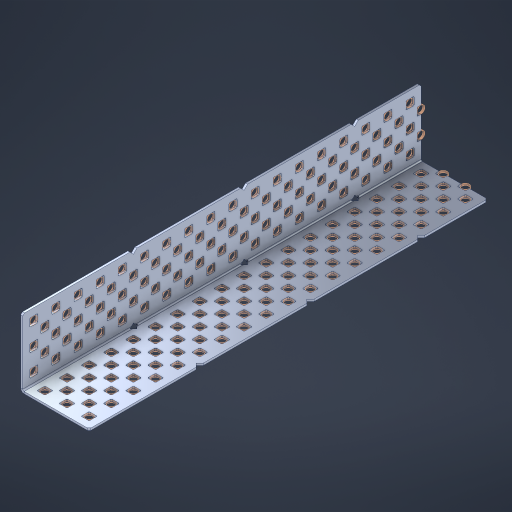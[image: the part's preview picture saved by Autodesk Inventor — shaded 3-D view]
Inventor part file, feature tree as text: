
AUTODESK INVENTOR PART (.ipt)
format: ipt  version: 2023 (Build 270158000, 158)  size: 2,013,184 bytes
history: native  units: in
note: dims shown in document units (in); Inventor stores cm internally (conversion verified against a paired STEP export)
features: other x186, extrude x178, sheet_metal_op x8, sketch x7, pattern_linear x3, mirror x1, chamfer x1
ambient origin geometry x8: Origin, YZ Plane, XZ Plane, XY Plane, X Axis, Y Axis, Z Axis, Center Point
bodies: Solid1 (feature_tree), Body (feature_tree)
feature tree (384):
  sheet_metal_op  "Flanges"
  sheet_metal_op  "Body Pattern"
  pattern_linear  "Center Double"  Spacing1=1.5in  [1 undecoded]
  pattern_linear  "Center Pattern"  Spacing1=0.1875in  [1 undecoded]
  other  "Arc Length"
  pattern_linear  "Notch Pattern"  Spacing1=0.0469in  [1 undecoded]
  other  "Diagonal Plane"
  mirror  "Everything Mirrored"
  chamfer  "End Chamfer"
  sketch  "Sketch1"  dims[d0=1.5in]
  other  "Plate1"
  sketch  "Sketch2"  dims[d1=9.0in]
  other  "Plate2"
  sheet_metal_op  "Bend1"
  sheet_metal_op  "Corner1"
  sketch  "Sketch8"  dims[d2=0.0469in]
  sketch  "Sketch9"  dims[d3=0.0469in]
  other  "Srf91"
  sheet_metal_op  "Body Pattern Sketch"
  other  "Srf92"
  sketch  "Sketch13"  dims[d4=0.0234in]
  sketch  "Sketch15"  dims[d5=0.0938in]
  sketch  "Sketch16"  dims[d6=0.0469in d7=1.5in d8=90.0deg d9=0.0312in d10=0.1875in d11=0.0469in d12=0.0469in d49=0.182in d50=0.02in d52=0.25in d53=0.0469in d54=0.0in d55=0.172in d56=1.0in d57=0.0in d85=0.1473in d86=0.1659in d89=0.0469in d90=0.0in d91=0.04in d92=0.0491in d95=2.5in d96=0.04in d97=0.25in d98=45.0deg d106=0.182in d107=0.02in d110=0.0469in d111=0.0in d112=0.172in d113=0.5in d114=0.0in d117=0.5in d126=0.0491in d127=0.1227in d128=0.08in d129=0.04in d130=2.5in d131=0.25in d132=7.0866in d134=0.5in d135=1.1811in d137=0.5in d140=0.5in d141=1.0in d142=0.3937in d144=0.5in d145=0.071in d146=0.7874in d148=0.5in]
  other  "Srf786"
  other  "Srf856"
  other  "Srf889"
  other  "Srf890"
  other  "Srf891"
  other  "Srf1275"
  other  "Srf1276"
  other  "Srf1278"
  other  "Srf1277"
  other  "Srf1285"
  other  "Srf1286"
  other  "Srf1287"
  other  "Srf1445"
  other  "Srf1446"
  other  "Srf1447"
  other  "Srf1448"
  other  "Srf1449"
  other  "Srf1537"
  other  "Srf1538"
  other  "Srf1539"
  other  "Srf1540"
  other  "Srf1541"
  other  "Srf1807"
  other  "Srf1808"
  other  "Srf1809"
  other  "Srf1810"
  other  "Srf1811"
  other  "Srf1812"
  other  "Srf1813"
  other  "Srf1814"
  other  "Srf1815"
  other  "Srf1959"
  other  "Srf1960"
  other  "Srf1961"
  other  "Srf1962"
  other  "Srf1963"
  other  "Srf1964"
  other  "Srf1965"
  other  "Srf1966"
  other  "Srf1967"
  other  "Srf2009"
  other  "Srf2010"
  other  "Srf2011"
  other  "Srf2012"
  other  "Srf2013"
  other  "Srf2014"
  other  "Srf2015"
  other  "Srf2016"
  other  "Srf2017"
  other  "Srf2018"
  other  "Srf2019"
  other  "Srf2020"
  other  "Srf2021"
  other  "Srf2022"
  other  "Srf2023"
  other  "Srf2024"
  other  "Srf2025"
  other  "Srf2026"
  other  "Srf2043"
  other  "Srf2044"
  other  "Srf2045"
  other  "Srf2046"
  other  "Srf2047"
  other  "Srf2048"
  other  "Srf2049"
  other  "Srf2050"
  other  "Srf2051"
  other  "Srf2052"
  other  "Srf2053"
  other  "Srf2054"
  other  "Srf2055"
  other  "Srf2056"
  other  "Srf2057"
  other  "Srf2058"
  other  "Srf2059"
  other  "Srf2076"
  other  "Srf2077"
  other  "Srf2078"
  other  "Srf2079"
  other  "Srf2080"
  other  "Srf2081"
  other  "Srf2082"
  other  "Srf2083"
  other  "Srf2084"
  other  "Srf2085"
  other  "Srf2086"
  other  "Srf2087"
  other  "Srf2088"
  other  "Srf2089"
  other  "Srf2090"
  other  "Srf2091"
  other  "Srf2092"
  other  "Srf2093"
  other  "Srf2094"
  other  "Srf2095"
  other  "Srf2096"
  other  "Srf2097"
  other  "Srf2098"
  other  "Srf2099"
  other  "Srf2100"
  other  "Srf2101"
  other  "Srf2102"
  other  "Srf2103"
  other  "Srf2104"
  other  "Srf2105"
  other  "Srf2106"
  other  "Srf2107"
  other  "Srf2108"
  other  "Srf2109"
  other  "Srf2110"
  other  "Srf2111"
  other  "Srf2112"
  other  "Srf2113"
  other  "Srf2114"
  other  "Srf2115"
  other  "Srf2116"
  other  "Srf2117"
  other  "Srf2118"
  other  "Srf2119"
  other  "Srf2120"
  other  "Srf2121"
  other  "Srf2122"
  other  "Srf2123"
  other  "Srf2124"
  other  "Srf2125"
  other  "Srf2126"
  other  "Srf2127"
  other  "Srf2179"
  other  "Srf2180"
  other  "Srf2181"
  other  "Srf2182"
  other  "Srf2183"
  other  "Srf2184"
  other  "Srf2185"
  other  "Srf2186"
  other  "Srf2187"
  other  "Srf2188"
  other  "Srf2189"
  other  "Srf2190"
  other  "Srf2191"
  other  "Srf2192"
  other  "Srf2193"
  other  "Srf2194"
  other  "Srf2195"
  other  "Srf2196"
  other  "Srf2197"
  other  "Srf2198"
  other  "Srf2199"
  other  "Srf2200"
  other  "Srf2201"
  other  "Srf2202"
  other  "Srf2203"
  other  "Srf2204"
  other  "Srf2205"
  other  "Srf2206"
  other  "Srf2207"
  other  "Srf2208"
  other  "Srf2209"
  other  "Srf2210"
  other  "Srf2211"
  other  "Srf2212"
  other  "Srf2213"
  other  "Srf2214"
  other  "Srf2215"
  other  "Srf2216"
  other  "Srf2217"
  other  "Srf2218"
  other  "Srf2219"
  other  "Srf2220"
  other  "Srf2221"
  other  "Srf2222"
  other  "Srf2223"
  other  "Srf2224"
  other  "Srf2225"
  other  "Srf2226"
  other  "Srf2227"
  other  "Srf2228"
  other  "Srf2229"
  sheet_metal_op  "Body Stamp"
  sheet_metal_op  "Body Circle"
  other  "Center Stamp"
  other  "Center Circle"
  sheet_metal_op  "Notch"
  extrude  "ExtrusionSrf92"  Depth=0.0469in
  extrude  "ExtrusionSrf856"  Depth=0.182in
  extrude  "ExtrusionSrf889"  Depth=0.02in
  extrude  "ExtrusionSrf890"  Depth=0.25in
  extrude  "ExtrusionSrf891"  Depth=0.0469in
  extrude  "ExtrusionSrf1275"  TaperAngle=0.0deg  [1 undecoded]
  extrude  "ExtrusionSrf1276"  Depth=0.5in
  extrude  "ExtrusionSrf1277"  Depth=1.0in TaperAngle=0.0deg
  extrude  "ExtrusionSrf1345"  Depth=0.5in
  extrude  "ExtrusionSrf1346"  Depth=0.5in
  extrude  "ExtrusionSrf1347"  Depth=0.0469in
  extrude  "ExtrusionSrf1348"  Depth=0.5in TaperAngle=0.0deg
  extrude  "ExtrusionSrf1445"  Depth=0.5in
  extrude  "ExtrusionSrf1446"  Depth=0.25in TaperAngle=45.0deg
  extrude  "ExtrusionSrf1447"  Depth=0.182in
  extrude  "ExtrusionSrf1448"  Depth=0.02in
  extrude  "ExtrusionSrf1449"  Depth=0.0469in
  extrude  "ExtrusionSrf1537"  TaperAngle=0.0deg  [1 undecoded]
  extrude  "ExtrusionSrf1538"  Depth=0.5in
  extrude  "ExtrusionSrf1539"  Depth=0.5in TaperAngle=0.0deg
  extrude  "ExtrusionSrf1540"  Depth=0.5in
  extrude  "ExtrusionSrf1541"  Depth=0.5in
  extrude  "ExtrusionSrf1807"  Depth=0.5in
  extrude  "ExtrusionSrf1808"  Depth=0.5in
  extrude  "ExtrusionSrf1809"  Depth=0.5in
  extrude  "ExtrusionSrf1810"  Depth=0.5in
  extrude  "ExtrusionSrf1811"  Depth=0.25in
  extrude  "ExtrusionSrf1812"  Depth=0.5in
  extrude  "ExtrusionSrf1813"  Depth=0.5in
  extrude  "ExtrusionSrf1814"  Depth=0.5in
  extrude  "ExtrusionSrf1815"  Depth=1.0in
  extrude  "ExtrusionSrf1959"  Depth=0.3937in
  extrude  "ExtrusionSrf1960"  Depth=0.5in
  extrude  "ExtrusionSrf1961"  Depth=0.5in
  extrude  "ExtrusionSrf1962"  [1 undecoded]
  extrude  "ExtrusionSrf1963"  [1 undecoded]
  extrude  "ExtrusionSrf1964"  [1 undecoded]
  extrude  "ExtrusionSrf1965"  [1 undecoded]
  extrude  "ExtrusionSrf1966"  [1 undecoded]
  extrude  "ExtrusionSrf1967"  [1 undecoded]
  extrude  "ExtrusionSrf2009"  [1 undecoded]
  extrude  "ExtrusionSrf2010"  [1 undecoded]
  extrude  "ExtrusionSrf2011"  [1 undecoded]
  extrude  "ExtrusionSrf2012"  [1 undecoded]
  extrude  "ExtrusionSrf2013"  [1 undecoded]
  extrude  "ExtrusionSrf2014"  [1 undecoded]
  extrude  "ExtrusionSrf2015"  [1 undecoded]
  extrude  "ExtrusionSrf2016"  [1 undecoded]
  extrude  "ExtrusionSrf2017"  [1 undecoded]
  extrude  "ExtrusionSrf2018"  [1 undecoded]
  extrude  "ExtrusionSrf2019"  [1 undecoded]
  extrude  "ExtrusionSrf2020"  [1 undecoded]
  extrude  "ExtrusionSrf2021"  [1 undecoded]
  extrude  "ExtrusionSrf2022"  [1 undecoded]
  extrude  "ExtrusionSrf2023"  [1 undecoded]
  extrude  "ExtrusionSrf2024"  [1 undecoded]
  extrude  "ExtrusionSrf2025"  [1 undecoded]
  extrude  "ExtrusionSrf2026"  [1 undecoded]
  extrude  "ExtrusionSrf2043"  [1 undecoded]
  extrude  "ExtrusionSrf2044"  [1 undecoded]
  extrude  "ExtrusionSrf2045"  [1 undecoded]
  extrude  "ExtrusionSrf2046"  [1 undecoded]
  extrude  "ExtrusionSrf2047"  [1 undecoded]
  extrude  "ExtrusionSrf2048"  [1 undecoded]
  extrude  "ExtrusionSrf2049"  [1 undecoded]
  extrude  "ExtrusionSrf2050"  [1 undecoded]
  extrude  "ExtrusionSrf2051"  [1 undecoded]
  extrude  "ExtrusionSrf2052"  [1 undecoded]
  extrude  "ExtrusionSrf2053"  [1 undecoded]
  extrude  "ExtrusionSrf2054"  [1 undecoded]
  extrude  "ExtrusionSrf2055"  [1 undecoded]
  extrude  "ExtrusionSrf2056"  [1 undecoded]
  extrude  "ExtrusionSrf2057"  [1 undecoded]
  extrude  "ExtrusionSrf2058"  [1 undecoded]
  extrude  "ExtrusionSrf2059"  [1 undecoded]
  extrude  "ExtrusionSrf2076"  [1 undecoded]
  extrude  "ExtrusionSrf2077"  [1 undecoded]
  extrude  "ExtrusionSrf2078"  [1 undecoded]
  extrude  "ExtrusionSrf2079"  [1 undecoded]
  extrude  "ExtrusionSrf2080"  [1 undecoded]
  extrude  "ExtrusionSrf2081"  [1 undecoded]
  extrude  "ExtrusionSrf2082"  [1 undecoded]
  extrude  "ExtrusionSrf2083"  [1 undecoded]
  extrude  "ExtrusionSrf2084"  [1 undecoded]
  extrude  "ExtrusionSrf2085"  [1 undecoded]
  extrude  "ExtrusionSrf2086"  [1 undecoded]
  extrude  "ExtrusionSrf2087"  [1 undecoded]
  extrude  "ExtrusionSrf2088"  [1 undecoded]
  extrude  "ExtrusionSrf2089"  [1 undecoded]
  extrude  "ExtrusionSrf2090"  [1 undecoded]
  extrude  "ExtrusionSrf2091"  [1 undecoded]
  extrude  "ExtrusionSrf2092"  [1 undecoded]
  extrude  "ExtrusionSrf2093"  [1 undecoded]
  extrude  "ExtrusionSrf2094"  [1 undecoded]
  extrude  "ExtrusionSrf2095"  [1 undecoded]
  extrude  "ExtrusionSrf2096"  [1 undecoded]
  extrude  "ExtrusionSrf2097"  [1 undecoded]
  extrude  "ExtrusionSrf2098"  [1 undecoded]
  extrude  "ExtrusionSrf2099"  [1 undecoded]
  extrude  "ExtrusionSrf2100"  [1 undecoded]
  extrude  "ExtrusionSrf2101"  [1 undecoded]
  extrude  "ExtrusionSrf2102"  [1 undecoded]
  extrude  "ExtrusionSrf2103"  [1 undecoded]
  extrude  "ExtrusionSrf2104"  [1 undecoded]
  extrude  "ExtrusionSrf2105"  [1 undecoded]
  extrude  "ExtrusionSrf2106"  [1 undecoded]
  extrude  "ExtrusionSrf2107"  [1 undecoded]
  extrude  "ExtrusionSrf2108"  [1 undecoded]
  extrude  "ExtrusionSrf2109"  [1 undecoded]
  extrude  "ExtrusionSrf2110"  [1 undecoded]
  extrude  "ExtrusionSrf2111"  [1 undecoded]
  extrude  "ExtrusionSrf2112"  [1 undecoded]
  extrude  "ExtrusionSrf2113"  [1 undecoded]
  extrude  "ExtrusionSrf2114"  [1 undecoded]
  extrude  "ExtrusionSrf2115"  [1 undecoded]
  extrude  "ExtrusionSrf2116"  [1 undecoded]
  extrude  "ExtrusionSrf2117"  [1 undecoded]
  extrude  "ExtrusionSrf2118"  [1 undecoded]
  extrude  "ExtrusionSrf2119"  [1 undecoded]
  extrude  "ExtrusionSrf2120"  [1 undecoded]
  extrude  "ExtrusionSrf2121"  [1 undecoded]
  extrude  "ExtrusionSrf2122"  [1 undecoded]
  extrude  "ExtrusionSrf2123"  [1 undecoded]
  extrude  "ExtrusionSrf2124"  [1 undecoded]
  extrude  "ExtrusionSrf2125"  [1 undecoded]
  extrude  "ExtrusionSrf2126"  [1 undecoded]
  extrude  "ExtrusionSrf2127"  [1 undecoded]
  extrude  "ExtrusionSrf2179"  [1 undecoded]
  extrude  "ExtrusionSrf2180"  [1 undecoded]
  extrude  "ExtrusionSrf2181"  [1 undecoded]
  extrude  "ExtrusionSrf2182"  [1 undecoded]
  extrude  "ExtrusionSrf2183"  [1 undecoded]
  extrude  "ExtrusionSrf2184"  [1 undecoded]
  extrude  "ExtrusionSrf2185"  [1 undecoded]
  extrude  "ExtrusionSrf2186"  [1 undecoded]
  extrude  "ExtrusionSrf2187"  [1 undecoded]
  extrude  "ExtrusionSrf2188"  [1 undecoded]
  extrude  "ExtrusionSrf2189"  [1 undecoded]
  extrude  "ExtrusionSrf2190"  [1 undecoded]
  extrude  "ExtrusionSrf2191"  [1 undecoded]
  extrude  "ExtrusionSrf2192"  [1 undecoded]
  extrude  "ExtrusionSrf2193"  [1 undecoded]
  extrude  "ExtrusionSrf2194"  [1 undecoded]
  extrude  "ExtrusionSrf2195"  [1 undecoded]
  extrude  "ExtrusionSrf2196"  [1 undecoded]
  extrude  "ExtrusionSrf2197"  [1 undecoded]
  extrude  "ExtrusionSrf2198"  [1 undecoded]
  extrude  "ExtrusionSrf2199"  [1 undecoded]
  extrude  "ExtrusionSrf2200"  [1 undecoded]
  extrude  "ExtrusionSrf2201"  [1 undecoded]
  extrude  "ExtrusionSrf2202"  [1 undecoded]
  extrude  "ExtrusionSrf2203"  [1 undecoded]
  extrude  "ExtrusionSrf2204"  [1 undecoded]
  extrude  "ExtrusionSrf2205"  [1 undecoded]
  extrude  "ExtrusionSrf2206"  [1 undecoded]
  extrude  "ExtrusionSrf2207"  [1 undecoded]
  extrude  "ExtrusionSrf2208"  [1 undecoded]
  extrude  "ExtrusionSrf2209"  [1 undecoded]
  extrude  "ExtrusionSrf2210"  [1 undecoded]
  extrude  "ExtrusionSrf2211"  [1 undecoded]
  extrude  "ExtrusionSrf2212"  [1 undecoded]
  extrude  "ExtrusionSrf2213"  [1 undecoded]
  extrude  "ExtrusionSrf2214"  [1 undecoded]
  extrude  "ExtrusionSrf2215"  [1 undecoded]
  extrude  "ExtrusionSrf2216"  [1 undecoded]
  extrude  "ExtrusionSrf2217"  [1 undecoded]
  extrude  "ExtrusionSrf2218"  [1 undecoded]
  extrude  "ExtrusionSrf2219"  [1 undecoded]
  extrude  "ExtrusionSrf2220"  [1 undecoded]
  extrude  "ExtrusionSrf2221"  [1 undecoded]
  extrude  "ExtrusionSrf2222"  [1 undecoded]
  extrude  "ExtrusionSrf2223"  [1 undecoded]
  extrude  "ExtrusionSrf2224"  [1 undecoded]
  extrude  "ExtrusionSrf2225"  [1 undecoded]
  extrude  "ExtrusionSrf2226"  [1 undecoded]
  extrude  "ExtrusionSrf2227"  [1 undecoded]
  extrude  "ExtrusionSrf2228"  [1 undecoded]
  extrude  "ExtrusionSrf2229"  [1 undecoded]
note: 149 required parameter values undecoded (feature->parameter linkage not recoverable at this tier; creation-order binding heuristic only, values carry confidence <= 0.55)
